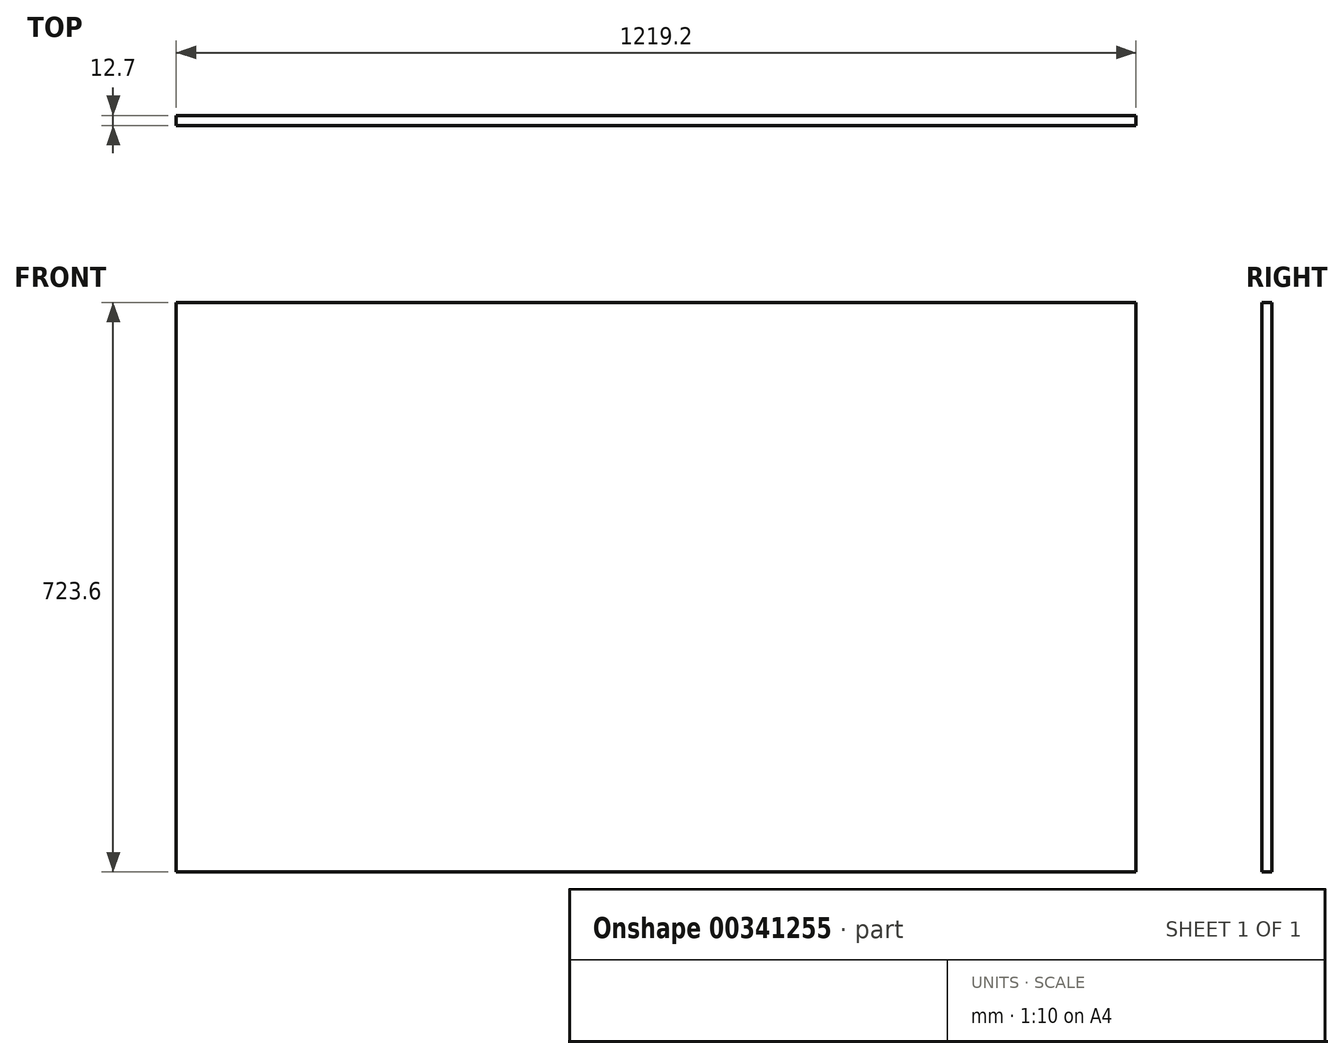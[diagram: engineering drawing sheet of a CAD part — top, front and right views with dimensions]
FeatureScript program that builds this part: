
annotation { "Feature Type Name" : "Feature", "Feature Type Description" : "" }
export const myFeature = defineFeature(function(context is Context, id is Id, definition is map)
    precondition{}
    {
        {
            var Q0;
            Q0=qCreatedBy(makeId("Front.planeOp"),FACE);
            var sketch = newSketch(context, id + "F0", { "sketchPlane" : qUnion([Q0])});
            skLineSegment(sketch, "E0.bottom", {"start": v(-609.6, 361.8) * mm, "end": v(609.6, 361.8) * mm});
            skLineSegment(sketch, "E0.top", {"start": v(-609.6, -361.8) * mm, "end": v(609.6, -361.8) * mm});
            skLineSegment(sketch, "E0.left", {"start": v(-609.6, 361.8) * mm, "end": v(-609.6, -361.8) * mm});
            skLineSegment(sketch, "E0.right", {"start": v(609.6, 361.8) * mm, "end": v(609.6, -361.8) * mm});
            skPoint(sketch, "E0.middle", {"position": v(0, 0) * mm});
            skSolve(sketch);
        }
        {
            var Q0;
            Q0=makeQuery(id+"F0.imprint","IMPRINT",FACE,{"disambiguationData":[TD([[makeQuery(id+"F0.imprint","IMPRINT",EDGE,{"derivedFrom":sQuery(id+"F0.wireOp",EDGE,"E0.bottom")}),-1.0]])]});
            extrude(context, id + "F1", {"entities" : qUnion([Q0]), "depth" : 12.7 * mm});
        }
    });
